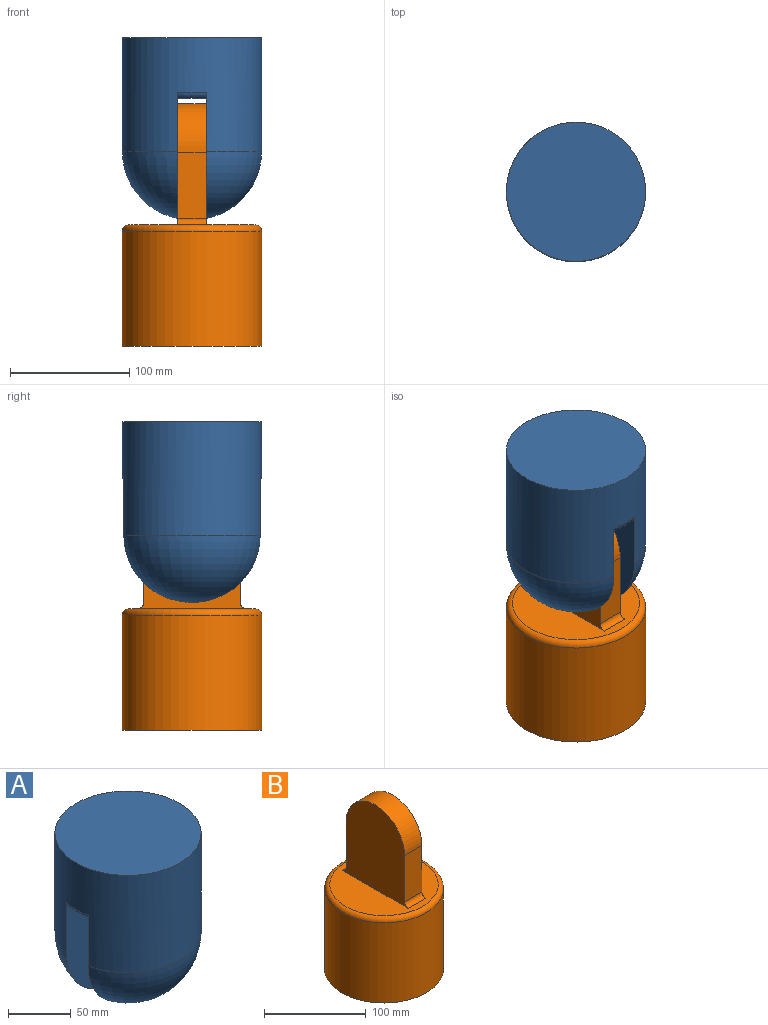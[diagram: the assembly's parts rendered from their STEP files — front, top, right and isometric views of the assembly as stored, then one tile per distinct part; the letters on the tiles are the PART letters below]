
ASSEMBLY  parts=2 mates=1
PART A: 9 faces, bbox 127x117.4x151.9 mm
  f0: plane 106.68x24.23mm, normal (0,0,-1), area 2562.5mm2, adj f3,f4,f7,f8
  f1: cylinder r=58.42mm len=116.84mm, axis (0,0,-1), area 32545mm2, adj f2,f3,f4,f5,f6,f7,f8
  f2: plane 116.84x116.84mm, normal (0,0,1), area 10721.9mm2, adj f1
  f3: plane 114.82x106.16mm, normal (0,-1,0), area 10146.8mm2, adj f0,f1,f5,f7,f8
  f4: plane 114.82x106.16mm, normal (0,1,0), area 10146.8mm2, adj f0,f1,f6,f7,f8
  f5: torus R=1.27mm, axis (0,0,-1), area 8416.3mm2, adj f1,f3
  f6: torus R=1.27mm, axis (0,0,-1), area 8416.3mm2, adj f1,f4
  f7: torus R=53.34mm, axis (0,0,1), area 197.6mm2, adj f0,f1,f3,f4
  f8: torus R=53.34mm, axis (0,0,1), area 197.6mm2, adj f0,f1,f3,f4
PART B: 11 faces, bbox 126.5x126.5x203.2 mm
  f0: plane 106.68x106.68mm, normal (0,0,1), area 6731.9mm2, adj f3,f5,f8,f9,f10
  f1: cylinder r=58.42mm len=116.84mm, axis (0,0,1), area 35429mm2, adj f2,f8
  f2: plane 116.84x116.84mm, normal (0,0,-1), area 10721.9mm2, adj f1
  f3: plane 101.6x91.44mm, normal (-1,0,0), area 7560.2mm2, adj f0,f4,f6,f7,f9,f10
  f4: plane 55.88x24.13mm, normal (0,-1,0), area 1348.4mm2, adj f3,f5,f7,f9
  f5: plane 101.6x91.44mm, normal (1,0,0), area 7560.2mm2, adj f0,f4,f6,f7,f9,f10
  f6: plane 55.88x24.13mm, normal (0,1,0), area 1348.4mm2, adj f3,f5,f7,f10
  f7: cylinder r=40.64mm len=81.28mm, axis (1,0,0), area 3080.8mm2, adj f3,f4,f5,f6
  f8: torus R=53.34mm, axis (0,0,1), area 2836.5mm2, adj f0,f1
  f9: cylinder r=5.08mm len=24.13mm, axis (1,0,0), area 192.5mm2, adj f0,f3,f4,f5
  f10: cylinder r=5.08mm len=24.13mm, axis (-1,0,0), area 192.5mm2, adj f0,f3,f5,f6
PLACE A rot(axis=(0,0,1),90deg) t=(116.56,32.03,52.93)mm
PLACE B t=(116.51,32.03,-53.19)mm
MATE revolute A.f3 <-> B.f7  axis (1,0,0) through (104.44,32.03,7.77)mm
